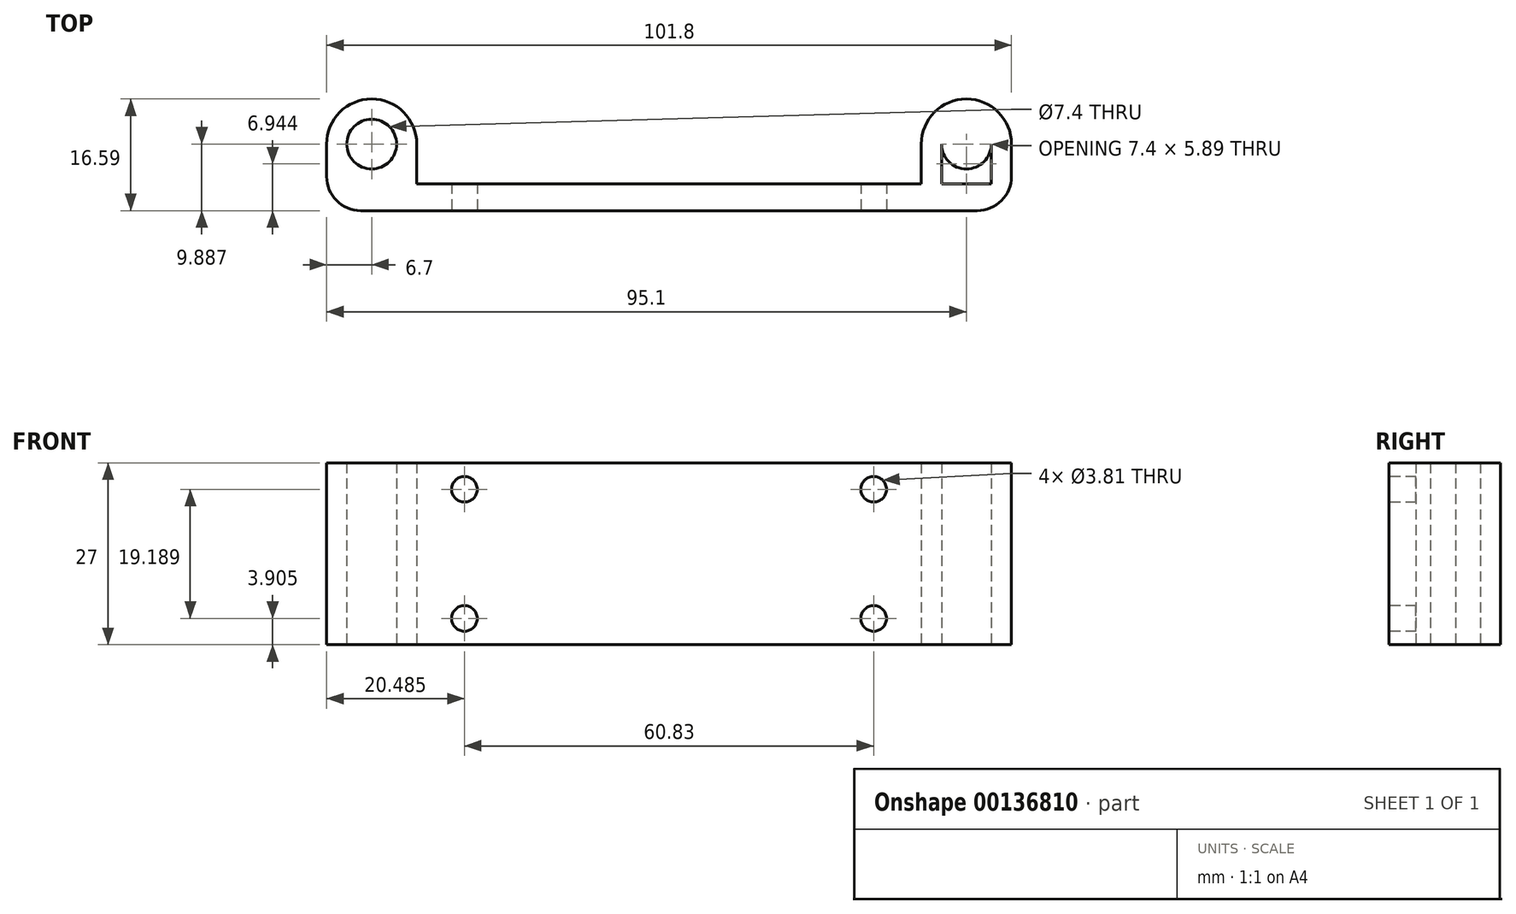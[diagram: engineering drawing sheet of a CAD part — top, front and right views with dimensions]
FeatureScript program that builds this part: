
annotation { "Feature Type Name" : "Feature", "Feature Type Description" : "" }
export const myFeature = defineFeature(function(context is Context, id is Id, definition is map)
    precondition{}
    {
        {
            var Q0;
            Q0=qCreatedBy(makeId("Top.planeOp"),FACE);
            var sketch = newSketch(context, id + "F0", { "sketchPlane" : qUnion([Q0])});
            skPoint(sketch, "E0.middle", {"position": v(0, 0) * mm});
            skCircle(sketch, "E1", {"center": v(-44.2, 7.89) * mm, "radius": 3.7 * mm});
            skCircle(sketch, "E2.MirrorC", {"center": v(44.2, 7.89) * mm, "radius": 3.7 * mm});
            skLineSegment(sketch, "E3", {"start": v(47.9, 7.89) * mm, "end": v(47.9, -2) * mm});
            skLineSegment(sketch, "E4", {"start": v(-47.9, -2) * mm, "end": v(47.9, -2) * mm});
            skLineSegment(sketch, "E5", {"start": v(0, -2) * mm, "end": v(0, 2) * mm});
            skLineSegment(sketch, "E6", {"start": v(0, 2) * mm, "end": v(47.9, 2) * mm});
            skLineSegment(sketch, "E7", {"start": v(0, 2) * mm, "end": v(-47.9, 2) * mm});
            skLineSegment(sketch, "E8", {"start": v(44.2, 7.89) * mm, "end": v(40.5, 7.89) * mm});
            skLineSegment(sketch, "E9", {"start": v(40.5, 7.89) * mm, "end": v(40.5, 2) * mm});
            skCircle(sketch, "E10", {"center": v(-44.2, 7.89) * mm, "radius": 6.7 * mm});
            skLineSegment(sketch, "E11", {"start": v(-37.5, 7.89) * mm, "end": v(-37.5, 2) * mm});
            skLineSegment(sketch, "E12", {"start": v(-50.9, 7.89) * mm, "end": v(-50.9, -2) * mm});
            skLineSegment(sketch, "E13", {"start": v(-50.9, -2) * mm, "end": v(-47.9, -2) * mm});
            skCircle(sketch, "E14.MirrorC", {"center": v(44.2, 7.89) * mm, "radius": 6.7 * mm});
            skLineSegment(sketch, "E15.MirrorCS", {"start": v(50.9, 7.89) * mm, "end": v(50.9, -2) * mm});
            skLineSegment(sketch, "E16.MirrorCS", {"start": v(50.9, -2) * mm, "end": v(47.9, -2) * mm});
            skLineSegment(sketch, "E17.MirrorCS", {"start": v(37.5, 7.89) * mm, "end": v(37.5, 2) * mm});
            skSolve(sketch);
        }
        {
            var Q0;
            Q0 = qSketchRegion(id + "F0", true);
            var Q1;
            {var subQ0=sQuery(id+"F0.wireOp",EDGE,"E10");var subQ1=sQuery(id+"F0.wireOp",EDGE,"E7");var subQ2=makeQuery(id+"F0.imprint","INTERSECT",VERTEX,{"disambiguationData":[OD(0.0)],"derivedFrom":[subQ1,subQ0]});Q1=makeQuery(id+"F0.imprint","IMPRINT",FACE,{"disambiguationData":[TD([[makeQuery(id+"F0.imprint","IMPRINT",EDGE,{"disambiguationData":[TD([[subQ2,1.0]])],"derivedFrom":subQ1}),1.0]])]});}
            var Q2;
            {var subQ5=sQuery(id+"F0.wireOp",EDGE,"E2.MirrorC");var subQ8=sQuery(id+"F0.wireOp",EDGE,"E3");var subQ9=makeQuery(id+"F0.imprint","INTERSECT",VERTEX,{"derivedFrom":[subQ5,subQ8]});Q2=makeQuery(id+"F0.imprint","IMPRINT",FACE,{"disambiguationData":[TD([[makeQuery(id+"F0.imprint","IMPRINT",EDGE,{"disambiguationData":[TD([[subQ9,-1.0]])],"derivedFrom":subQ5}),1.0]])]});}
            var Q3;
            {var subQ0=sQuery(id+"F0.wireOp",EDGE,"E14.MirrorC");var subQ1=sQuery(id+"F0.wireOp",EDGE,"E6");var subQ2=makeQuery(id+"F0.imprint","INTERSECT",VERTEX,{"disambiguationData":[OD(0.0)],"derivedFrom":[subQ1,subQ0]});Q3=makeQuery(id+"F0.imprint","IMPRINT",FACE,{"disambiguationData":[TD([[makeQuery(id+"F0.imprint","IMPRINT",EDGE,{"disambiguationData":[TD([[subQ2,-1.0]])],"derivedFrom":subQ1}),-1.0]])]});}
            extrude(context, id + "F1", {"entities" : qUnion([Q0, Q1, Q2, Q3]), "endBound" : BoundingType.SYMMETRIC, "depth" : 27 * mm});
        }
        {
            var Q0;
            Q0=makeQuery(id+"F1.opExtrude","SWEPT_EDGE",EDGE,{"disambiguationData":[OSD([sQuery(id+"F0.wireOp",EDGE,"E15.MirrorCS"),sQuery(id+"F0.wireOp",EDGE,"E16.MirrorCS")])]});
            var Q1;
            Q1=makeQuery(id+"F1.opExtrude","SWEPT_EDGE",EDGE,{"disambiguationData":[OSD([sQuery(id+"F0.wireOp",EDGE,"E12"),sQuery(id+"F0.wireOp",EDGE,"E13")])]});
            fillet(context, id + "F2", {"entities" : qUnion([Q0, Q1]), "radius" : 5.08 * mm, "tangentPropagation" : true, "allowEdgeOverflow" : false});
        }
        {
            var Q0;
            Q0=makeQuery(id+"F1.opExtrude","SWEPT_FACE",FACE,{"disambiguationData":[OSD([sQuery(id+"F0.wireOp",EDGE,"E4"),sQuery(id+"F0.wireOp",EDGE,"E13"),sQuery(id+"F0.wireOp",EDGE,"E16.MirrorCS")])]});
            var sketch = newSketch(context, id + "F3", { "sketchPlane" : qUnion([Q0])});
            skLineSegment(sketch, "E18.bottom", {"start": v(30.42, 9.6) * mm, "end": v(-30.42, 9.6) * mm});
            skLineSegment(sketch, "E18.top", {"start": v(30.42, -9.6) * mm, "end": v(-30.42, -9.6) * mm});
            skLineSegment(sketch, "E18.left", {"start": v(30.42, 9.6) * mm, "end": v(30.42, -9.6) * mm});
            skLineSegment(sketch, "E18.right", {"start": v(-30.42, 9.6) * mm, "end": v(-30.42, -9.6) * mm});
            skPoint(sketch, "E18.middle", {"position": v(0, 0) * mm});
            skSolve(sketch);
        }
        {
            var Q0;
            Q0=sQuery(id+"F3.wireOp",VERTEX,"E18.right.start");
            var Q1;
            Q1=sQuery(id+"F3.wireOp",VERTEX,"E18.right.end");
            var Q2;
            Q2=sQuery(id+"F3.wireOp",VERTEX,"E18.left.end");
            var Q3;
            Q3=sQuery(id+"F3.wireOp",VERTEX,"E18.bottom.start");
            var Q4;
            Q4=makeQuery(id+"F1.opExtrude","SWEPT_BODY",BODY,{"disambiguationData":[OSD([sQuery(id+"F0.wireOp",EDGE,"E1"),sQuery(id+"F0.wireOp",EDGE,"E2.MirrorC"),sQuery(id+"F0.wireOp",EDGE,"E3"),sQuery(id+"F0.wireOp",EDGE,"E4"),sQuery(id+"F0.wireOp",EDGE,"E6"),sQuery(id+"F0.wireOp",EDGE,"E7"),sQuery(id+"F0.wireOp",EDGE,"E9"),sQuery(id+"F0.wireOp",EDGE,"E10"),sQuery(id+"F0.wireOp",EDGE,"E11"),sQuery(id+"F0.wireOp",EDGE,"E12"),sQuery(id+"F0.wireOp",EDGE,"E13"),sQuery(id+"F0.wireOp",EDGE,"E14.MirrorC"),sQuery(id+"F0.wireOp",EDGE,"E15.MirrorCS"),sQuery(id+"F0.wireOp",EDGE,"E16.MirrorCS"),sQuery(id+"F0.wireOp",EDGE,"E17.MirrorCS")])]});
            hole(context, id + "F4", {"style" : HoleStyle.SIMPLE, "endStyle" : HoleEndStyle.THROUGH, "holeDiameter" : 3.8 * mm, "locations" : qUnion([Q0, Q1, Q2, Q3]), "scope" : qUnion([Q4]), "isTappedThrough" : true});
        }
    });
